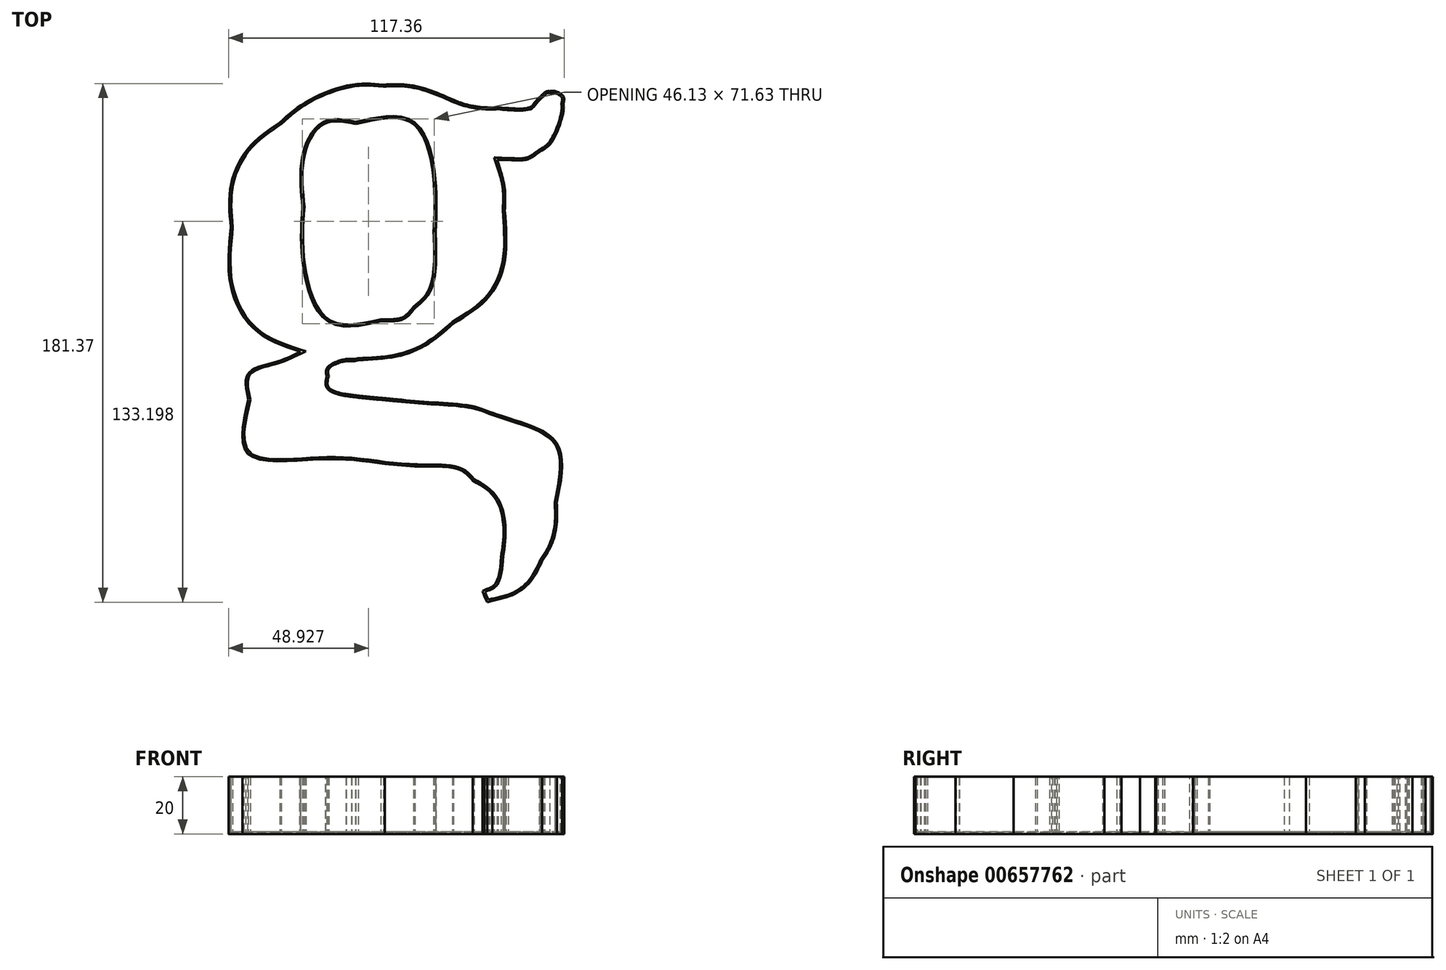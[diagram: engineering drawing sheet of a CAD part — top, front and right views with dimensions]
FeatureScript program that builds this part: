
annotation { "Feature Type Name" : "Feature", "Feature Type Description" : "" }
export const myFeature = defineFeature(function(context is Context, id is Id, definition is map)
    precondition{}
    {
        {
            var Q0;
            Q0=qCreatedBy(makeId("Top.planeOp"),FACE);
            var sketch = newSketch(context, id + "F0", { "sketchPlane" : qUnion([Q0])});
            skLineSegment(sketch, "E0", {"start": v(-59.77, -25.17) * mm, "end": v(-59.77, -22.53) * mm});
            skFitSpline(sketch, "E1", {"points": [v(-14.92, 76.24) * mm, v(5.21, 76.24) * mm, v(12.35, 55.87) * mm, v(12.35, 38.42) * mm]});
            skFitSpline(sketch, "E2", {"points": [v(12.35, 38.42) * mm, v(12.35, 25.63) * mm, v(10.04, 17.1) * mm, v(5.29, 12.35) * mm]});
            skFitSpline(sketch, "E3", {"points": [v(5.29, 12.35) * mm, v(1.64, 8.7) * mm, v(-2.93, 7.93) * mm, v(-6.13, 7.93) * mm]});
            skFitSpline(sketch, "E4", {"points": [v(-6.13, 7.93) * mm, v(-24.46, 7.93) * mm, v(-32.8, 28.3) * mm, v(-32.8, 47.22) * mm]});
            skFitSpline(sketch, "E5", {"points": [v(-32.8, 47.22) * mm, v(-32.8, 65.12) * mm, v(-25.95, 76.24) * mm, v(-14.92, 76.24) * mm]});
            skFitSpline(sketch, "E6", {"points": [v(49.64, 66.64) * mm, v(53.71, 69.97) * mm, v(57.74, 80.61) * mm, v(57.74, 83.25) * mm]});
            skFitSpline(sketch, "E7", {"points": [v(57.74, 83.25) * mm, v(57.74, 85.92) * mm, v(54.86, 87.7) * mm, v(52.96, 87.7) * mm]});
            skFitSpline(sketch, "E8", {"points": [v(52.96, 87.7) * mm, v(52.1, 87.7) * mm, v(51.3, 87.37) * mm, v(50.72, 86.78) * mm]});
            skFitSpline(sketch, "E9", {"points": [v(50.72, 86.78) * mm, v(47.76, 83.84) * mm, v(45.97, 82.06) * mm, v(34.89, 82.06) * mm]});
            skFitSpline(sketch, "E10", {"points": [v(34.89, 82.06) * mm, v(29.98, 82.06) * mm, v(23.12, 83.24) * mm, v(18.97, 84.8) * mm]});
            skFitSpline(sketch, "E11", {"points": [v(18.97, 84.8) * mm, v(10.12, 88.34) * mm, v(2.42, 89.98) * mm, v(-5.25, 89.98) * mm]});
            skFitSpline(sketch, "E12", {"points": [v(-5.25, 89.98) * mm, v(-15.98, 89.98) * mm, v(-31.83, 84.17) * mm, v(-41.36, 76.73) * mm]});
            skFitSpline(sketch, "E13", {"points": [v(-41.36, 76.73) * mm, v(-52.3, 67.86) * mm, v(-58.56, 54.54) * mm, v(-58.56, 40.18) * mm]});
            skFitSpline(sketch, "E14", {"points": [v(-58.56, 40.18) * mm, v(-58.56, 19.57) * mm, v(-49.77, 3.96) * mm, v(-34.24, -3.41) * mm]});
            skFitSpline(sketch, "E15", {"points": [v(-34.24, -3.41) * mm, v(-34.33, -3.45) * mm, v(-34.42, -3.49) * mm, v(-34.5, -3.52) * mm]});
            skFitSpline(sketch, "E16", {"points": [v(-34.5, -3.52) * mm, v(-42.9, -7.03) * mm, v(-52.4, -11) * mm, v(-52.4, -20.18) * mm]});
            skFitSpline(sketch, "E17", {"points": [v(-52.4, -20.18) * mm, v(-52.4, -39.18) * mm, v(-27.06, -41.02) * mm, v(-4.66, -42.66) * mm]});
            skFitSpline(sketch, "E18", {"points": [v(-4.66, -42.66) * mm, v(7.97, -43.57) * mm, v(21.02, -44.52) * mm, v(26.05, -48.52) * mm]});
            skFitSpline(sketch, "E19", {"points": [v(26.05, -48.52) * mm, v(34.09, -54.92) * mm, v(36.8, -66.5) * mm, v(35.94, -75.13) * mm]});
            skFitSpline(sketch, "E20", {"points": [v(35.94, -75.13) * mm, v(35.37, -80.7) * mm, v(33.5, -85.06) * mm, v(31, -86.34) * mm]});
            skFitSpline(sketch, "E21", {"points": [v(32.83, -90.5) * mm, v(40.46, -88.27) * mm, v(46.35, -83.59) * mm, v(50.33, -76.59) * mm]});
            skFitSpline(sketch, "E22", {"points": [v(50.33, -76.59) * mm, v(53.6, -70.86) * mm, v(55.4, -63.63) * mm, v(55.4, -56.23) * mm]});
            skFitSpline(sketch, "E23", {"points": [v(55.4, -56.23) * mm, v(55.4, -35.35) * mm, v(40.73, -27.36) * mm, v(31.95, -24.44) * mm]});
            skFitSpline(sketch, "E24", {"points": [v(31.95, -24.44) * mm, v(25.26, -22.34) * mm, v(10.96, -21.06) * mm, v(-1.74, -19.93) * mm]});
            skFitSpline(sketch, "E25", {"points": [v(-1.74, -19.93) * mm, v(-7.17, -19.44) * mm, v(-12.8, -18.94) * mm, v(-16.26, -18.47) * mm]});
            skFitSpline(sketch, "E26", {"points": [v(-16.26, -18.47) * mm, v(-19.38, -18.02) * mm, v(-24.31, -15.87) * mm, v(-24.31, -11.98) * mm]});
            skFitSpline(sketch, "E27", {"points": [v(-24.31, -11.98) * mm, v(-24.31, -9.44) * mm, v(-20.39, -7.21) * mm, v(-18.2, -6.7) * mm]});
            skFitSpline(sketch, "E28", {"points": [v(-18.2, -6.7) * mm, v(-16.73, -6.7) * mm, v(-15.2, -6.68) * mm, v(-13.91, -6.37) * mm]});
            skFitSpline(sketch, "E29", {"points": [v(-13.91, -6.37) * mm, v(-0.72, -5.1) * mm, v(9.87, -1) * mm, v(19.35, 6.5) * mm]});
            skFitSpline(sketch, "E30", {"points": [v(19.35, 6.5) * mm, v(31.38, 15.52) * mm, v(37.23, 28.45) * mm, v(37.23, 46.04) * mm]});
            skFitSpline(sketch, "E31", {"points": [v(37.23, 46.04) * mm, v(37.23, 53.48) * mm, v(35.81, 59.82) * mm, v(34.54, 63.72) * mm]});
            skFitSpline(sketch, "E32", {"points": [v(34.54, 63.72) * mm, v(36.16, 63.64) * mm, v(36.85, 63.64) * mm, v(38.41, 63.64) * mm]});
            skFitSpline(sketch, "E33", {"points": [v(38.41, 63.64) * mm, v(44.29, 63.64) * mm, v(46.94, 64.7) * mm, v(49.64, 66.64) * mm]});
            skLineSegment(sketch, "E34", {"start": v(31, -86.34) * mm, "end": v(29.41, -87.16) * mm});
            skLineSegment(sketch, "E35", {"start": v(29.41, -87.16) * mm, "end": v(30.07, -88.82) * mm});
            skLineSegment(sketch, "E36", {"start": v(30.07, -88.82) * mm, "end": v(31.1, -91.02) * mm});
            skLineSegment(sketch, "E37", {"start": v(31.1, -91.02) * mm, "end": v(32.83, -90.5) * mm});
            skSolve(sketch);
        }
        {
            var Q0;
            Q0=makeQuery(id+"F0.imprint","IMPRINT",FACE,{"disambiguationData":[TD([[makeQuery(id+"F0.imprint","IMPRINT",EDGE,{"derivedFrom":sQuery(id+"F0.wireOp",EDGE,"E1")}),1.0]])]});
            extrude(context, id + "F1", {"entities" : qUnion([Q0]), "depth" : 20 * mm, "offsetDistance" : 25 * mm});
        }
        {
            var Q0;
            Q0=makeQuery(id+"F1.opExtrude","CAP_FACE",FACE,{"disambiguationData":[OSD([sQuery(id+"F0.wireOp",EDGE,"E1"),sQuery(id+"F0.wireOp",EDGE,"E2"),sQuery(id+"F0.wireOp",EDGE,"E3"),sQuery(id+"F0.wireOp",EDGE,"E4"),sQuery(id+"F0.wireOp",EDGE,"E5"),sQuery(id+"F0.wireOp",EDGE,"E6"),sQuery(id+"F0.wireOp",EDGE,"E7"),sQuery(id+"F0.wireOp",EDGE,"E8"),sQuery(id+"F0.wireOp",EDGE,"E9"),sQuery(id+"F0.wireOp",EDGE,"E10"),sQuery(id+"F0.wireOp",EDGE,"E11"),sQuery(id+"F0.wireOp",EDGE,"E12"),sQuery(id+"F0.wireOp",EDGE,"E13"),sQuery(id+"F0.wireOp",EDGE,"E14"),sQuery(id+"F0.wireOp",EDGE,"E15"),sQuery(id+"F0.wireOp",EDGE,"E16"),sQuery(id+"F0.wireOp",EDGE,"E17"),sQuery(id+"F0.wireOp",EDGE,"E18"),sQuery(id+"F0.wireOp",EDGE,"E19"),sQuery(id+"F0.wireOp",EDGE,"E20"),sQuery(id+"F0.wireOp",EDGE,"E21"),sQuery(id+"F0.wireOp",EDGE,"E22"),sQuery(id+"F0.wireOp",EDGE,"E23"),sQuery(id+"F0.wireOp",EDGE,"E24"),sQuery(id+"F0.wireOp",EDGE,"E25"),sQuery(id+"F0.wireOp",EDGE,"E26"),sQuery(id+"F0.wireOp",EDGE,"E27"),sQuery(id+"F0.wireOp",EDGE,"E28"),sQuery(id+"F0.wireOp",EDGE,"E29"),sQuery(id+"F0.wireOp",EDGE,"E30"),sQuery(id+"F0.wireOp",EDGE,"E31"),sQuery(id+"F0.wireOp",EDGE,"E32"),sQuery(id+"F0.wireOp",EDGE,"E33"),sQuery(id+"F0.wireOp",EDGE,"E34"),sQuery(id+"F0.wireOp",EDGE,"E35"),sQuery(id+"F0.wireOp",EDGE,"E36"),sQuery(id+"F0.wireOp",EDGE,"E37")])],"isStart":false});
            shell(context, id + "F2", {"entities" : qUnion([Q0]), "thickness" : 0.7 * mm});
        }
    });
